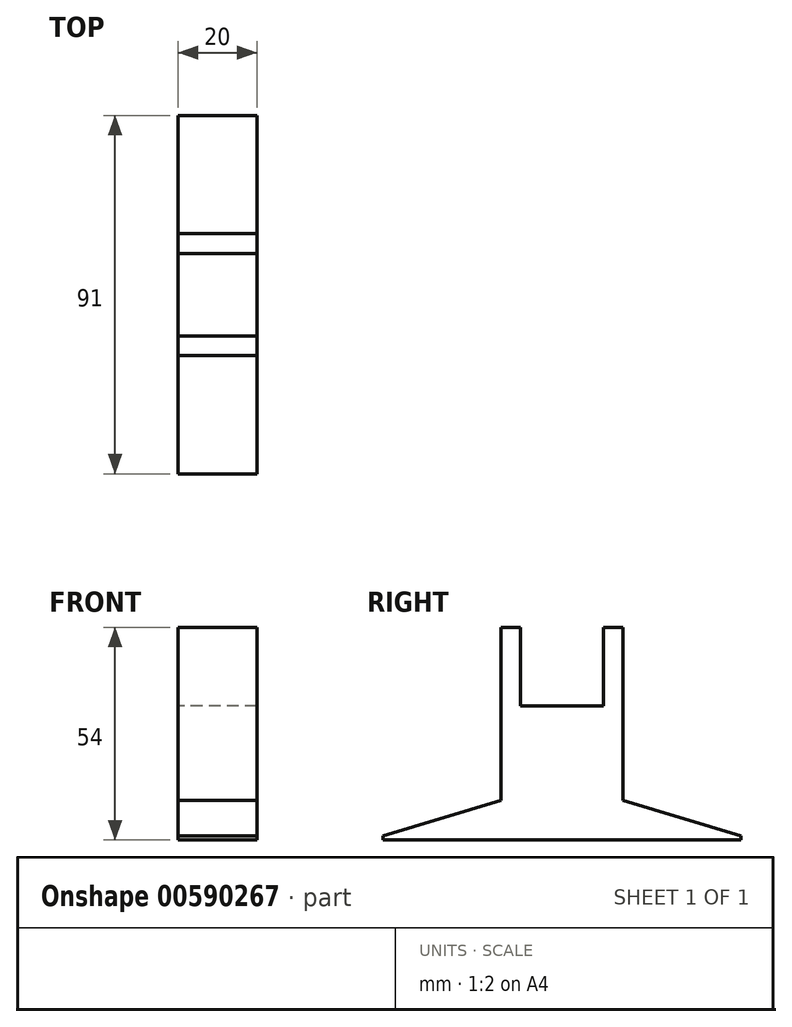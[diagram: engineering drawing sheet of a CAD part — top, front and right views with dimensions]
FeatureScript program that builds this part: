
annotation { "Feature Type Name" : "Feature", "Feature Type Description" : "" }
export const myFeature = defineFeature(function(context is Context, id is Id, definition is map)
    precondition{}
    {
        {
            var Q0;
            Q0=qCreatedBy(makeId("Top.planeOp"),FACE);
            var sketch = newSketch(context, id + "F0", { "sketchPlane" : qUnion([Q0])});
            skLineSegment(sketch, "E0.bottom", {"start": v(0, 0) * mm, "end": v(20, 0) * mm});
            skLineSegment(sketch, "E0.top", {"start": v(0, 31) * mm, "end": v(20, 31) * mm});
            skLineSegment(sketch, "E0.left", {"start": v(0, 0) * mm, "end": v(0, 31) * mm});
            skLineSegment(sketch, "E0.right", {"start": v(20, 0) * mm, "end": v(20, 31) * mm});
            skSolve(sketch);
        }
        {
            var Q0;
            Q0 = qSketchRegion(id + "F0", true);
            extrude(context, id + "F1", {"entities" : qUnion([Q0]), "depth" : 34 * mm, "offsetDistance" : 25 * mm});
        }
        {
            var Q0;
            Q0=makeQuery(id+"F1.opExtrude","CAP_FACE",FACE,{"disambiguationData":[OSD([sQuery(id+"F0.wireOp",EDGE,"E0.bottom"),sQuery(id+"F0.wireOp",EDGE,"E0.top"),sQuery(id+"F0.wireOp",EDGE,"E0.left"),sQuery(id+"F0.wireOp",EDGE,"E0.right")])],"isStart":false});
            var sketch = newSketch(context, id + "F2", { "sketchPlane" : qUnion([Q0])});
            skLineSegment(sketch, "E1.bottom", {"start": v(0, 31) * mm, "end": v(20, 31) * mm});
            skLineSegment(sketch, "E1.top", {"start": v(0, 26) * mm, "end": v(20, 26) * mm});
            skLineSegment(sketch, "E1.left", {"start": v(0, 31) * mm, "end": v(0, 26) * mm});
            skLineSegment(sketch, "E1.right", {"start": v(20, 31) * mm, "end": v(20, 26) * mm});
            skLineSegment(sketch, "E2.bottom", {"start": v(20, 0) * mm, "end": v(0, 0) * mm});
            skLineSegment(sketch, "E2.top", {"start": v(20, 5) * mm, "end": v(0, 5) * mm});
            skLineSegment(sketch, "E2.left", {"start": v(20, 0) * mm, "end": v(20, 5) * mm});
            skLineSegment(sketch, "E2.right", {"start": v(0, 0) * mm, "end": v(0, 5) * mm});
            skSolve(sketch);
        }
        {
            var Q0;
            Q0 = qSketchRegion(id + "F2", true);
            extrude(context, id + "F3", {"entities" : qUnion([Q0]), "operationType" : NewBodyOperationType.ADD, "depth" : 20 * mm, "offsetDistance" : 25 * mm});
        }
        {
            var Q0;
            Q0=makeQuery(id+"F3.boolean.opBoolean","MERGE",FACE,{"derivedFrom":[makeQuery(id+"F1.opExtrude","SWEPT_FACE",FACE,{"disambiguationData":[OSD([sQuery(id+"F0.wireOp",EDGE,"E0.bottom")])]}),makeQuery(id+"F3.opExtrude","SWEPT_FACE",FACE,{"disambiguationData":[OSD([sQuery(id+"F2.wireOp",EDGE,"E2.bottom")])]})]});
            var sketch = newSketch(context, id + "F4", { "sketchPlane" : qUnion([Q0])});
            skLineSegment(sketch, "E3.bottom", {"start": v(0, 0) * mm, "end": v(20, 0) * mm});
            skLineSegment(sketch, "E3.top", {"start": v(0, 10) * mm, "end": v(20, 10) * mm});
            skLineSegment(sketch, "E3.left", {"start": v(0, 0) * mm, "end": v(0, 10) * mm});
            skLineSegment(sketch, "E3.right", {"start": v(20, 0) * mm, "end": v(20, 10) * mm});
            skSolve(sketch);
        }
        {
            var Q0;
            Q0 = qSketchRegion(id + "F4", true);
            extrude(context, id + "F5", {"entities" : qUnion([Q0]), "operationType" : NewBodyOperationType.ADD, "depth" : 30 * mm, "offsetDistance" : 25 * mm});
        }
        {
            var Q0;
            Q0=makeQuery(id+"F3.boolean.opBoolean","MERGE",FACE,{"derivedFrom":[makeQuery(id+"F1.opExtrude","SWEPT_FACE",FACE,{"disambiguationData":[OSD([sQuery(id+"F0.wireOp",EDGE,"E0.top")])]}),makeQuery(id+"F3.opExtrude","SWEPT_FACE",FACE,{"disambiguationData":[OSD([sQuery(id+"F2.wireOp",EDGE,"E1.bottom")])]})]});
            var sketch = newSketch(context, id + "F6", { "sketchPlane" : qUnion([Q0])});
            skLineSegment(sketch, "E4.bottom", {"start": v(-20, 0) * mm, "end": v(0, 0) * mm});
            skLineSegment(sketch, "E4.top", {"start": v(-20, 10) * mm, "end": v(0, 10) * mm});
            skLineSegment(sketch, "E4.left", {"start": v(-20, 0) * mm, "end": v(-20, 10) * mm});
            skLineSegment(sketch, "E4.right", {"start": v(0, 0) * mm, "end": v(0, 10) * mm});
            skSolve(sketch);
        }
        {
            var Q0;
            Q0 = qSketchRegion(id + "F6", true);
            extrude(context, id + "F7", {"entities" : qUnion([Q0]), "operationType" : NewBodyOperationType.ADD, "depth" : 30 * mm, "offsetDistance" : 25 * mm});
        }
        {
            var Q0;
            Q0=makeQuery(id+"F7.boolean.opBoolean","MERGE",FACE,{"derivedFrom":[makeQuery(id+"F5.boolean.opBoolean","MERGE",FACE,{"derivedFrom":[makeQuery(id+"F3.boolean.opBoolean","MERGE",FACE,{"derivedFrom":[makeQuery(id+"F1.opExtrude","SWEPT_FACE",FACE,{"disambiguationData":[OSD([sQuery(id+"F0.wireOp",EDGE,"E0.right")])]}),makeQuery(id+"F3.opExtrude","SWEPT_FACE",FACE,{"disambiguationData":[OSD([sQuery(id+"F2.wireOp",EDGE,"E1.right")])]}),makeQuery(id+"F3.opExtrude","SWEPT_FACE",FACE,{"disambiguationData":[OSD([sQuery(id+"F2.wireOp",EDGE,"E2.left")])]})]}),makeQuery(id+"F5.opExtrude","SWEPT_FACE",FACE,{"disambiguationData":[OSD([sQuery(id+"F4.wireOp",EDGE,"E3.right")])]})]}),makeQuery(id+"F7.opExtrude","SWEPT_FACE",FACE,{"disambiguationData":[OSD([sQuery(id+"F6.wireOp",EDGE,"E4.left")])]})]});
            var sketch = newSketch(context, id + "F8", { "sketchPlane" : qUnion([Q0])});
            skLineSegment(sketch, "E5", {"start": v(0, 10) * mm, "end": v(-30, 1) * mm});
            skLineSegment(sketch, "E6", {"start": v(-30, 1) * mm, "end": v(-30, 10) * mm});
            skLineSegment(sketch, "E7", {"start": v(-30, 10) * mm, "end": v(0, 10) * mm});
            skLineSegment(sketch, "E8", {"start": v(31, 10) * mm, "end": v(61, 10) * mm});
            skLineSegment(sketch, "E9", {"start": v(61, 10) * mm, "end": v(61, 1) * mm});
            skLineSegment(sketch, "E10", {"start": v(61, 1) * mm, "end": v(31, 10) * mm});
            skSolve(sketch);
        }
        {
            var Q0;
            Q0=makeQuery(id+"F8.imprint","IMPRINT",FACE,{"disambiguationData":[TD([[makeQuery(id+"F8.imprint","IMPRINT",EDGE,{"derivedFrom":sQuery(id+"F8.wireOp",EDGE,"E5")}),-1.0]])]});
            var Q1;
            Q1=makeQuery(id+"F8.imprint","IMPRINT",FACE,{"disambiguationData":[TD([[makeQuery(id+"F8.imprint","IMPRINT",EDGE,{"derivedFrom":sQuery(id+"F8.wireOp",EDGE,"E8")}),1.0]])]});
            extrude(context, id + "F9", {"entities" : qUnion([Q0, Q1]), "operationType" : NewBodyOperationType.REMOVE, "oppositeDirection" : true, "depth" : 20 * mm, "offsetDistance" : 25 * mm});
        }
    });
